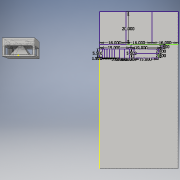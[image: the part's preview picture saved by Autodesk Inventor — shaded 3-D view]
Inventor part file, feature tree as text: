
AUTODESK INVENTOR PART (.ipt)
format: ipt  version: 2016 (Build 200138000, 138)  size: 250,368 bytes
history: native  units: in
note: dims shown in document units (in); Inventor stores cm internally (conversion verified against a paired STEP export)
features: sketch x10, extrude x8, plane x1, loft x1
ambient origin geometry x8: Origin, YZ Plane, XZ Plane, XY Plane, X Axis, Y Axis, Z Axis, Center Point
bodies: Solid1 (feature_tree)
feature tree (20):
  extrude  "Extrusion1"  Depth=20.0in
  sketch  "Sketch2"  dims[d2=16.0in d3=0.0in d4=11.75in]
  plane  "Work Plane1"
  loft  "Loft1"
  extrude  "Extrusion2"  Depth=6.5in
  extrude  "Extrusion3"  TaperAngle=0.0deg  [1 undecoded]
  extrude  "Extrusion4"  Depth=13.3in
  extrude  "Extrusion5"  Depth=2.56in
  extrude  "Extrusion6"  Depth=15.3775in TaperAngle=0.0deg
  extrude  "Extrusion7"  Depth=5.5in TaperAngle=0.0deg
  extrude  "Extrusion8"  Depth=1.0in TaperAngle=0.0deg
  sketch  "Sketch11"  dims[d30=1.0in d31=1.0in d32=1.0in d33=1.0in d34=2.8in d35=0.0in d36=1.0in d37=16.0in d38=0.0in d39=48.0in d40=96.0in d41=0.75in d42=0.0in d43=20.0in d44=16.0in d45=16.0in d46=16.0in d47=2.8in d48=19.0in d49=19.0in d53=5.5in d54=1.5in d55=1.5in d56=1.5in d57=1.5in d58=1.5in d59=1.5in d60=3.0in d61=3.0in d62=3.0in d63=3.0in d64=5.5in d65=15.0in d66=2.8in d67=2.8in]
  sketch  "Sketch1"  dims[d0=1.0in d1=20.0in]
  sketch  "Sketch3"  dims[d5=6.5in d6=2.5in]
  sketch  "Sketch4"  dims[d7=0.0in d8=90.0deg d9=0.0in d10=90.0deg]
  sketch  "Sketch6"  dims[d11=16.2in d12=13.3in]
  sketch  "Sketch7"  dims[d13=2.56in d14=0.0in d15=0.94in]
  sketch  "Sketch8"  dims[d16=8.1in d17=15.3775in d18=0.0in]
  sketch  "Sketch9"  dims[d19=3.0in d20=5.5in d21=0.0in]
  sketch  "Sketch10"  dims[d22=1.25in d23=1.25in d24=1.25in d25=1.25in d26=1.25in d27=1.25in d28=1.0in d29=0.0in]
note: 1 required parameter value undecoded (feature->parameter linkage not recoverable at this tier; creation-order binding heuristic only, values carry confidence <= 0.55)
